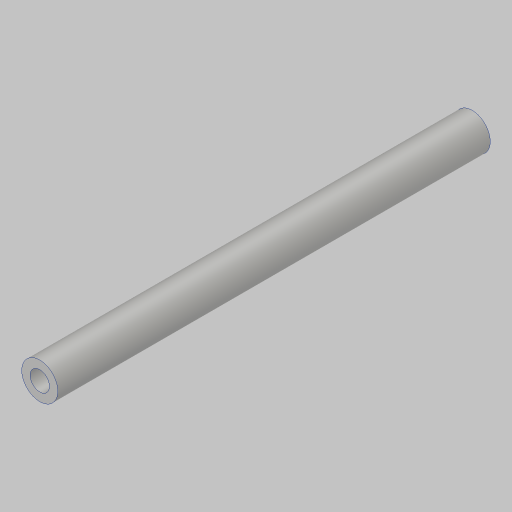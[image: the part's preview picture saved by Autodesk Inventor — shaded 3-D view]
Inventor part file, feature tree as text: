
AUTODESK INVENTOR PART (.ipt)
format: ipt  version: 2023.5 (Build 275446000, 446)  size: 96,256 bytes
history: native  units: in
note: dims shown in document units (in); Inventor stores cm internally (conversion verified against a paired STEP export)
features: extrude x1, hole x1
ambient origin geometry x8: Origin, YZ Plane, XZ Plane, XY Plane, X Axis, Y Axis, Z Axis, Center Point
bodies: Solid1 (feature_tree)
feature tree (2):
  extrude  "Extrusion1"  Depth=4.5in
  hole  "Hole1"  [1 undecoded]
note: 1 required parameter value undecoded (feature->parameter linkage not recoverable at this tier; creation-order binding heuristic only, values carry confidence <= 0.55)
